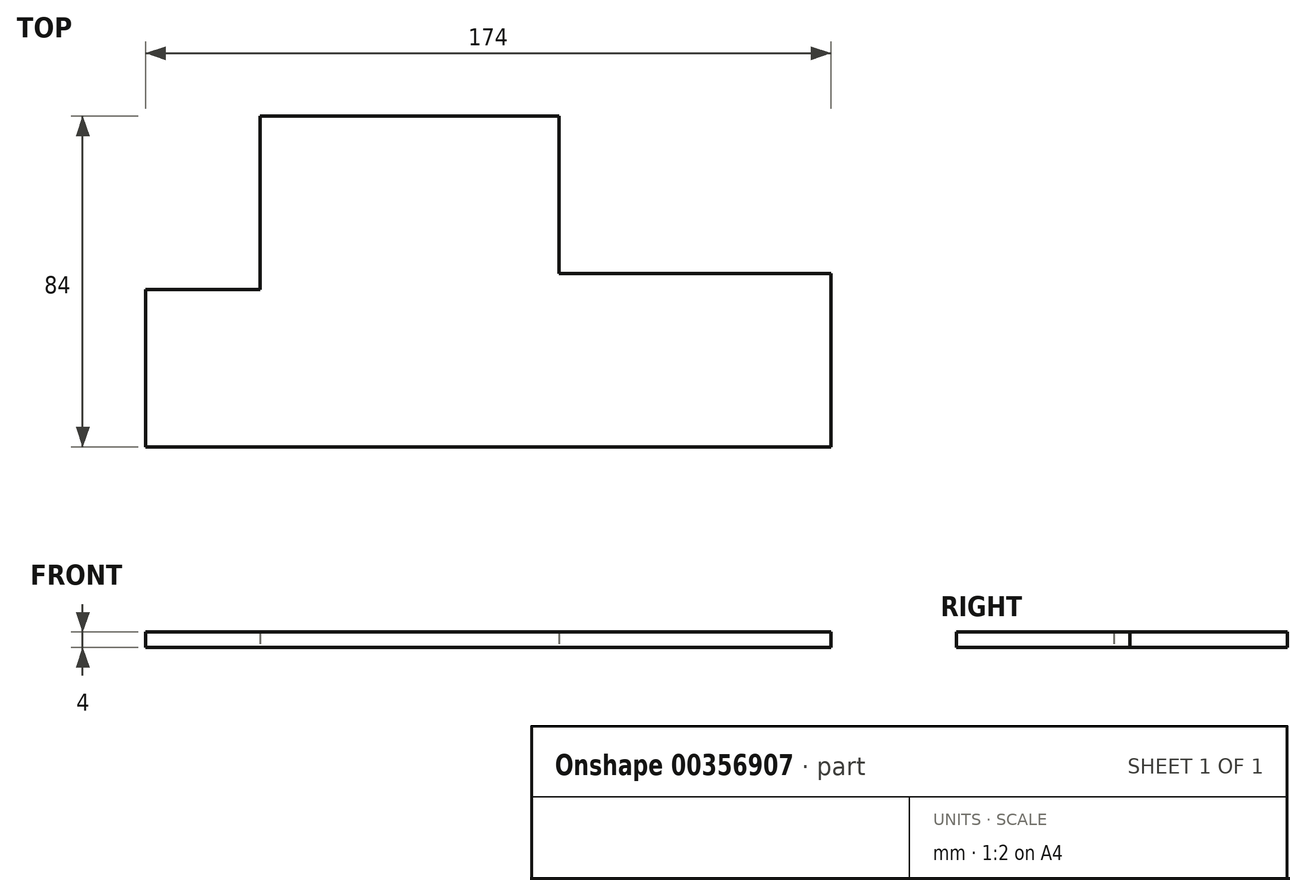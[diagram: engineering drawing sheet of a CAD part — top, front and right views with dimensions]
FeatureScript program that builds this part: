
annotation { "Feature Type Name" : "Feature", "Feature Type Description" : "" }
export const myFeature = defineFeature(function(context is Context, id is Id, definition is map)
    precondition{}
    {
        {
            var Q0;
            Q0=qCreatedBy(makeId("Top.planeOp"),FACE);
            var sketch = newSketch(context, id + "F0", { "sketchPlane" : qUnion([Q0])});
            skLineSegment(sketch, "E0.bottom", {"start": v(-56, 44) * mm, "end": v(20, 44) * mm});
            skLineSegment(sketch, "E0.top", {"start": v(-85, -40) * mm, "end": v(89, -40) * mm});
            skLineSegment(sketch, "E0.left", {"start": v(-85, 0) * mm, "end": v(-85, -40) * mm});
            skLineSegment(sketch, "E0.right", {"start": v(89, 4) * mm, "end": v(89, -40) * mm});
            skPoint(sketch, "E0.middle", {"position": v(0, 0) * mm});
            skLineSegment(sketch, "E1", {"start": v(-56, 44) * mm, "end": v(-56, 0) * mm});
            skLineSegment(sketch, "E2", {"start": v(20, 44) * mm, "end": v(20, 4) * mm});
            skLineSegment(sketch, "E3", {"start": v(-56, 0) * mm, "end": v(-85, 0) * mm});
            skLineSegment(sketch, "E4", {"start": v(20, 4) * mm, "end": v(89, 4) * mm});
            skSolve(sketch);
        }
        {
            var Q0;
            Q0=qSketchRegion(id+"F0",true);
            extrude(context, id + "F1", {"entities" : qUnion([Q0]), "depth" : 4 * mm});
        }
    });
